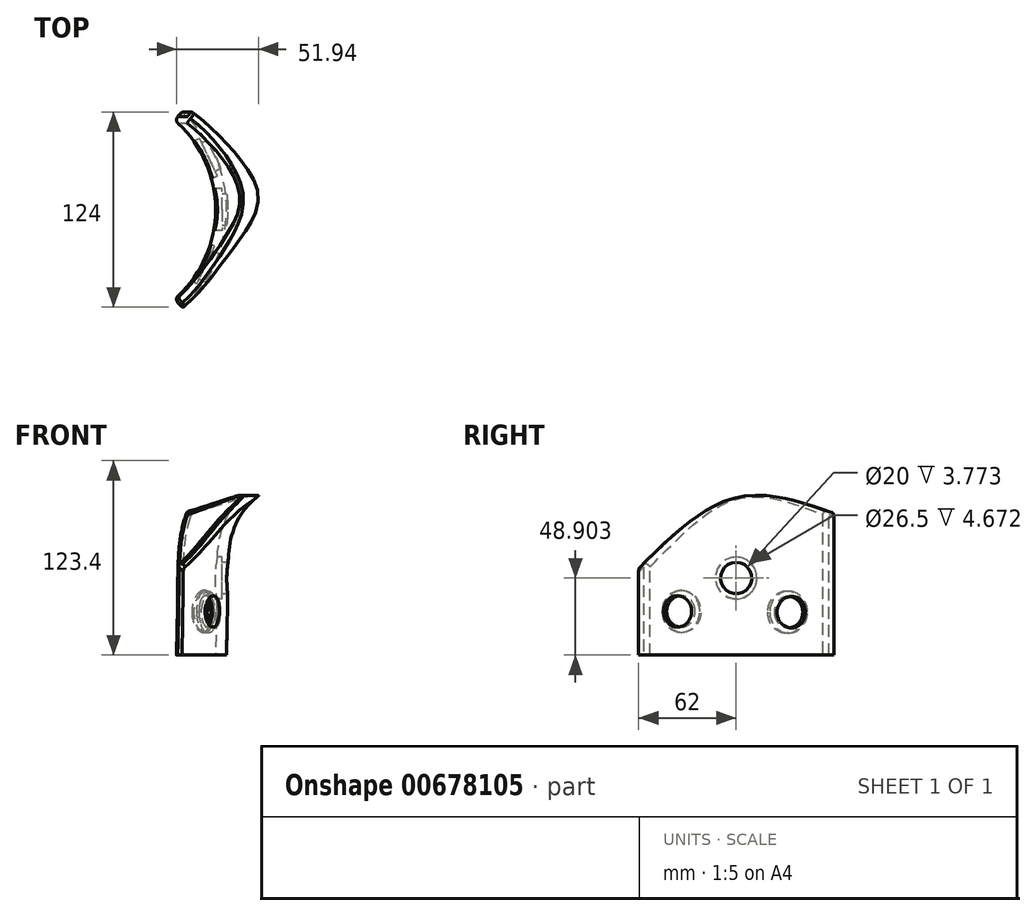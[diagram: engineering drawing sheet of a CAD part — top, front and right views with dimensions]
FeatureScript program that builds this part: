
annotation { "Feature Type Name" : "Feature", "Feature Type Description" : "" }
export const myFeature = defineFeature(function(context is Context, id is Id, definition is map)
    precondition{}
    {
        {
            var Q0;
            Q0=qCreatedBy(makeId("Top.planeOp"),FACE);
            var sketch = newSketch(context, id + "F0", { "sketchPlane" : qUnion([Q0])});
            skCircle(sketch, "E0", {"center": v(0, 0) * mm, "radius": 75 * mm});
            skCircle(sketch, "E1", {"center": v(0, 0) * mm, "radius": 82 * mm});
            skLineSegment(sketch, "E2", {"start": v(0, 0) * mm, "end": v(53.67, 62) * mm});
            skLineSegment(sketch, "E3", {"start": v(0, 0) * mm, "end": v(53.67, -62) * mm});
            skLineSegment(sketch, "E4", {"start": v(53.67, -62) * mm, "end": v(53.67, 62) * mm, "construction": true});
            skPoint(sketch, "E5", {"position": v(75, 0) * mm});
            skSolve(sketch);
        }
        {
            var Q0;
            Q0=qCreatedBy(makeId("Front.planeOp"),FACE);
            var sketch = newSketch(context, id + "F1", { "sketchPlane" : qUnion([Q0])});
            skLineSegment(sketch, "E6.0", {"start": v(-75, 0) * mm, "end": v(75, 0) * mm, "construction": true});
            skLineSegment(sketch, "E7.0", {"start": v(-82, 0) * mm, "end": v(82, 0) * mm, "construction": true});
            skPoint(sketch, "E8.0", {"position": v(53.67, 0) * mm});
            skLineSegment(sketch, "E9", {"start": v(75, 0) * mm, "end": v(82, 0) * mm, "construction": true});
            skPoint(sketch, "E10", {"position": v(78.5, 0) * mm});
            skFitSpline(sketch, "E11", {"points": [v(78.5, 0) * mm, v(79.69, 61.38) * mm, v(111.07, 110) * mm], "startDerivative": vector(7, 296.95) * mm, "endDerivative": vector(173.88, 79.92) * mm});
            skSolve(sketch);
        }
        {
            var Q0;
            {var subQ0=sQuery(id+"F0.wireOp",EDGE,"E2");var subQ1=sQuery(id+"F0.wireOp",EDGE,"E0");var subQ2=makeQuery(id+"F0.imprint","INTERSECT",VERTEX,{"derivedFrom":[subQ1,subQ0]});Q0=makeQuery(id+"F0.imprint","IMPRINT",FACE,{"disambiguationData":[TD([[makeQuery(id+"F0.imprint","IMPRINT",EDGE,{"disambiguationData":[TD([[subQ2,1.0]])],"derivedFrom":subQ1}),-1.0]])]});}
            var Q1;
            Q1=sQuery(id+"F1.wireOp",EDGE,"E11");
            sweep(context, id + "F2", {"profiles" : qUnion([Q0]), "path" : qUnion([Q1])});
        }
        {
            var Q0;
            Q0=makeQuery(id+"F2.opSweep","SWEPT_EDGE",EDGE,{"disambiguationData":[OSD([sQuery(id+"F0.wireOp",EDGE,"E1"),sQuery(id+"F0.wireOp",EDGE,"E3"),sQuery(id+"F1.wireOp",EDGE,"E11")])]});
            cPoint(context, id + "F3", {"entities" : qUnion([Q0]), "parameter" : 0.5});
        }
        {
            var Q0;
            Q0=qCreatedBy(makeId("Front.planeOp"),FACE);
            var Q1;
            Q1 = qCreatedBy(id + "F3" ,VERTEX);
            cPlane(context, id + "F4", {"entities" : qUnion([Q0, Q1]), "cplaneType" : CPlaneType.PLANE_POINT, "offset" : 25 * mm, "width" : 150 * mm, "height" : 150 * mm});
        }
        {
            var Q0;
            Q0=qCreatedBy(id+"F4.planeOp",FACE);
            var sketch = newSketch(context, id + "F5", { "sketchPlane" : qUnion([Q0])});
            skLineSegment(sketch, "E12", {"start": v(16.14, 55) * mm, "end": v(159.54, 55) * mm});
            skLineSegment(sketch, "E13.top", {"start": v(16.14, 155) * mm, "end": v(159.54, 155) * mm});
            skLineSegment(sketch, "E13.left", {"start": v(16.14, 55) * mm, "end": v(16.14, 155) * mm});
            skLineSegment(sketch, "E13.right", {"start": v(159.54, 55) * mm, "end": v(159.54, 155) * mm});
            skSolve(sketch);
        }
        {
            var Q0;
            Q0=qCreatedBy(makeId("Right.planeOp"),FACE);
            var sketch = newSketch(context, id + "F6", { "sketchPlane" : qUnion([Q0])});
            skPoint(sketch, "E14.0", {"position": v(-62, 55) * mm});
            skLineSegment(sketch, "E15", {"start": v(-62, 55) * mm, "end": v(-129.5, 55) * mm, "construction": true});
            skLineSegment(sketch, "E16", {"start": v(-62, 55) * mm, "end": v(3.7, 55) * mm, "construction": true});
            skFitSpline(sketch, "E17.0", {"points": [v(62, 0) * mm, v(1000, 62) * mm, v(14.52, 1000) * mm, v(62, 21.04) * mm, v(1000, 62) * mm, v(27.13, 1000) * mm, v(62, 28.59) * mm, v(1000, 62) * mm, v(31.82, 1000) * mm, v(62, 33.54) * mm, v(1000, 62) * mm, v(38.98, 1000) * mm, v(62, 43.59) * mm, v(1000, 62) * mm, v(54.54, 1000) * mm, v(62, 60.9) * mm, v(1000, 62) * mm, v(74.53, 1000) * mm], "construction": true});
            skFitSpline(sketch, "E18.0", {"points": [v(-62, 0) * mm, v(1000, -62) * mm, v(14.52, 1000) * mm, v(-62, 21.04) * mm, v(1000, -62) * mm, v(27.13, 1000) * mm, v(-62, 28.59) * mm, v(1000, -62) * mm, v(31.82, 1000) * mm, v(-62, 33.54) * mm, v(1000, -62) * mm, v(38.98, 1000) * mm, v(-62, 43.59) * mm, v(1000, -62) * mm, v(54.54, 1000) * mm, v(-62, 60.9) * mm, v(1000, -62) * mm, v(74.53, 1000) * mm], "construction": true});
            skLineSegment(sketch, "E19", {"start": v(68.45, 90) * mm, "end": v(-5.43, 90) * mm, "construction": true});
            skLineSegment(sketch, "E20", {"start": v(40.28, 100) * mm, "end": v(-42.7, 100) * mm, "construction": true});
            skFitSpline(sketch, "E21", {"points": [v(62, 90) * mm, v(0, 100) * mm, v(-62, 55) * mm], "startDerivative": vector(-133.41, 46.42) * mm, "endDerivative": vector(-114.9, -113.77) * mm});
            skSolve(sketch);
        }
        {
            var Q0;
            Q0=makeQuery(id+"F5.imprint","IMPRINT",FACE,{"disambiguationData":[TD([[makeQuery(id+"F5.imprint","IMPRINT",EDGE,{"derivedFrom":sQuery(id+"F5.wireOp",EDGE,"E12")}),1.0]])]});
            var Q1;
            Q1=sQuery(id+"F6.wireOp",EDGE,"E21");
            sweep(context, id + "F7", {"operationType" : NewBodyOperationType.REMOVE, "profiles" : qUnion([Q0]), "path" : qUnion([Q1]), "keepProfileOrientation" : true});
        }
        {
            var Q0;
            Q0=makeQuery(id+"F7.boolean.opBoolean","INTERSECT",EDGE,{"derivedFrom":[makeQuery(id+"F2.opSweep","SWEPT_FACE",FACE,{"disambiguationData":[OSD([sQuery(id+"F0.wireOp",EDGE,"E0"),sQuery(id+"F1.wireOp",EDGE,"E11")])]}),makeQuery(id+"F7.opSweep","SWEPT_FACE",FACE,{"disambiguationData":[OSD([sQuery(id+"F5.wireOp",EDGE,"E12"),sQuery(id+"F6.wireOp",EDGE,"E21")])]})]});
            fillet(context, id + "F8", {"entities" : qUnion([Q0]), "radius" : 3 * mm, "tangentPropagation" : true, "allowEdgeOverflow" : false});
        }
        {
            var Q0;
            Q0=makeQuery(id+"F2.opSweep","SWEPT_EDGE",EDGE,{"disambiguationData":[OSD([sQuery(id+"F0.wireOp",EDGE,"E0"),sQuery(id+"F0.wireOp",EDGE,"E2"),sQuery(id+"F1.wireOp",EDGE,"E11")])]});
            var Q1;
            Q1=makeQuery(id+"F2.opSweep","SWEPT_EDGE",EDGE,{"disambiguationData":[OSD([sQuery(id+"F0.wireOp",EDGE,"E0"),sQuery(id+"F0.wireOp",EDGE,"E3"),sQuery(id+"F1.wireOp",EDGE,"E11")])]});
            fillet(context, id + "F9", {"entities" : qUnion([Q0, Q1]), "radius" : 3 * mm, "tangentPropagation" : true, "allowEdgeOverflow" : false});
        }
        {
            var Q0;
            Q0=sQuery(id+"F0.wireOp",EDGE,"E4");
            cPoint(context, id + "F10", {"entities" : qUnion([Q0]), "parameter" : 0.5});
        }
        {
            var Q0;
            Q0=qCreatedBy(makeId("Right.planeOp"),FACE);
            var Q1;
            Q1 = qCreatedBy(id + "F10" ,VERTEX);
            cPlane(context, id + "F11", {"entities" : qUnion([Q0, Q1]), "cplaneType" : CPlaneType.PLANE_POINT, "offset" : 25 * mm, "width" : 150 * mm, "height" : 150 * mm});
        }
        {
            var Q0;
            Q0=qCreatedBy(makeId("Top.planeOp"),FACE);
            var sketch = newSketch(context, id + "F12", { "sketchPlane" : qUnion([Q0])});
            skCircle(sketch, "E22", {"center": v(0, 0) * mm, "radius": 82 * mm});
            skLineSegment(sketch, "E23", {"start": v(0, 0) * mm, "end": v(74.16, 35) * mm});
            skLineSegment(sketch, "E24", {"start": v(0, 0) * mm, "end": v(74.16, -35) * mm});
            skLineSegment(sketch, "E25", {"start": v(74.16, -35) * mm, "end": v(74.16, 35) * mm, "construction": true});
            skPoint(sketch, "E26", {"position": v(75, 0) * mm});
            skFitSpline(sketch, "E27.0", {"points": [v(78.5, 0) * mm, v(78.91, 0) * mm, v(78.47, 0) * mm, v(79.8, 0) * mm, v(91.34, 0) * mm], "construction": true});
            skSolve(sketch);
        }
        {
            var Q0;
            Q0=sQuery(id+"F12.wireOp",VERTEX,"E22.center");
            var Q1;
            Q1=sQuery(id+"F12.wireOp",EDGE,"E23");
            cPlane(context, id + "F13", {"entities" : qUnion([Q0, Q1]), "cplaneType" : CPlaneType.LINE_POINT, "offset" : 25 * mm, "width" : 150 * mm, "height" : 150 * mm});
        }
        {
            var Q0;
            Q0=qCreatedBy(id+"F13.planeOp",FACE);
            var sketch = newSketch(context, id + "F14", { "sketchPlane" : qUnion([Q0])});
            skCircle(sketch, "E28", {"center": v(0, 27.24) * mm, "radius": 10 * mm});
            skCircle(sketch, "E29", {"center": v(0, 27.24) * mm, "radius": 13.25 * mm});
            skSolve(sketch);
        }
        {
            var Q0;
            Q0=sQuery(id+"F12.wireOp",EDGE,"E24");
            var Q1;
            Q1=sQuery(id+"F12.wireOp",VERTEX,"E22.center");
            cPlane(context, id + "F15", {"entities" : qUnion([Q0, Q1]), "cplaneType" : CPlaneType.LINE_POINT, "offset" : 25 * mm, "width" : 150 * mm, "height" : 150 * mm});
        }
        {
            var Q0;
            Q0=qCreatedBy(id+"F15.planeOp",FACE);
            var sketch = newSketch(context, id + "F16", { "sketchPlane" : qUnion([Q0])});
            skCircle(sketch, "E30", {"center": v(-2.46, 27.68) * mm, "radius": 10 * mm});
            skCircle(sketch, "E31", {"center": v(-2.46, 27.68) * mm, "radius": 13.25 * mm});
            skSolve(sketch);
        }
        {
            var Q0;
            Q0=qCreatedBy(id+"F11.planeOp",FACE);
            var sketch = newSketch(context, id + "F17", { "sketchPlane" : qUnion([Q0])});
            skCircle(sketch, "E32", {"center": v(0, 48.9) * mm, "radius": 10 * mm});
            skCircle(sketch, "E33", {"center": v(0, 48.9) * mm, "radius": 13.25 * mm});
            skSolve(sketch);
        }
        {
            var Q0;
            Q0=makeQuery(id+"F14.imprint","IMPRINT",FACE,{"disambiguationData":[TD([[makeQuery(id+"F14.imprint","IMPRINT",EDGE,{"derivedFrom":sQuery(id+"F14.wireOp",EDGE,"E28")}),1.0]])]});
            extrude(context, id + "F18", {"entities" : qUnion([Q0]), "operationType" : NewBodyOperationType.REMOVE, "depth" : 100 * mm, "offsetDistance" : 25 * mm});
        }
        {
            var Q0;
            Q0=makeQuery(id+"F16.imprint","IMPRINT",FACE,{"disambiguationData":[TD([[makeQuery(id+"F16.imprint","IMPRINT",EDGE,{"derivedFrom":sQuery(id+"F16.wireOp",EDGE,"E30")}),1.0]])]});
            extrude(context, id + "F19", {"entities" : qUnion([Q0]), "operationType" : NewBodyOperationType.REMOVE, "depth" : 100 * mm, "offsetDistance" : 25 * mm});
        }
        {
            var Q0;
            Q0=makeQuery(id+"F17.imprint","IMPRINT",FACE,{"disambiguationData":[TD([[makeQuery(id+"F17.imprint","IMPRINT",EDGE,{"derivedFrom":sQuery(id+"F17.wireOp",EDGE,"E32")}),1.0]])]});
            extrude(context, id + "F20", {"entities" : qUnion([Q0]), "operationType" : NewBodyOperationType.REMOVE, "depth" : 100 * mm, "offsetDistance" : 25 * mm});
        }
        {
            var Q0;
            Q0=makeQuery(id+"F16.imprint","IMPRINT",FACE,{"disambiguationData":[TD([[makeQuery(id+"F16.imprint","IMPRINT",EDGE,{"derivedFrom":sQuery(id+"F16.wireOp",EDGE,"E30")}),-1.0]])]});
            extrude(context, id + "F21", {"entities" : qUnion([Q0]), "operationType" : NewBodyOperationType.REMOVE, "depth" : (74.07 + 3) * mm, "offsetDistance" : 25 * mm});
        }
        {
            var Q0;
            Q0=makeQuery(id+"F17.imprint","IMPRINT",FACE,{"disambiguationData":[TD([[makeQuery(id+"F17.imprint","IMPRINT",EDGE,{"derivedFrom":sQuery(id+"F17.wireOp",EDGE,"E32")}),-1.0]])]});
            extrude(context, id + "F22", {"entities" : qUnion([Q0]), "operationType" : NewBodyOperationType.REMOVE, "depth" : (22.6 + 3) * mm, "offsetDistance" : 25 * mm});
        }
        {
            var Q0;
            Q0=makeQuery(id+"F14.imprint","IMPRINT",FACE,{"disambiguationData":[TD([[makeQuery(id+"F14.imprint","IMPRINT",EDGE,{"derivedFrom":sQuery(id+"F14.wireOp",EDGE,"E28")}),-1.0]])]});
            extrude(context, id + "F23", {"entities" : qUnion([Q0]), "operationType" : NewBodyOperationType.REMOVE, "depth" : (74.92 + 3) * mm, "offsetDistance" : 25 * mm});
        }
    });
